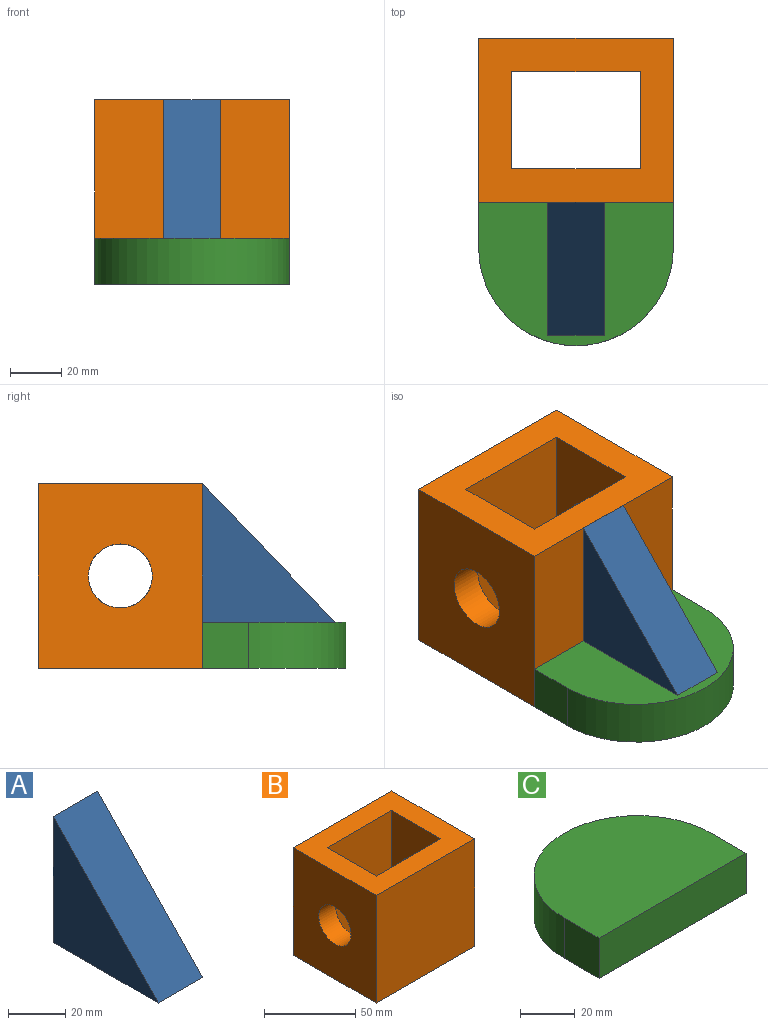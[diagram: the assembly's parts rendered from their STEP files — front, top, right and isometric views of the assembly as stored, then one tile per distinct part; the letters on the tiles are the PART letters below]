
ASSEMBLY  parts=3 mates=2
PART A: 5 faces, bbox 22x52x54 mm
  f0: plane 54x52mm, normal (0,-0.72,0.69), area 1649.3mm2, adj f1,f2,f3,f4
  f1: plane 52x22mm, normal (0,0,-1), area 1144mm2, adj f0,f2,f3,f4
  f2: plane 54x22mm, normal (0,1,0), area 1188mm2, adj f0,f1,f3,f4
  f3: plane 54x52mm, normal (1,0,0), area 1404mm2, adj f0,f1,f2
  f4: plane 54x52mm, normal (-1,0,0), area 1404mm2, adj f0,f1,f2
PART B: 12 faces, bbox 76x64x72 mm
  f0: plane 76x72mm, normal (0,-1,0), area 5472mm2, adj f1,f7,f8,f9
  f1: plane 72x64mm, normal (1,0,0), area 4117.1mm2, adj f0,f2,f8,f9,f11
  f2: plane 76x72mm, normal (0,1,0), area 5472mm2, adj f1,f7,f8,f9
  f3: plane 72x50mm, normal (0,-1,0), area 3600mm2, adj f4,f6,f8,f9
  f4: plane 72x38mm, normal (-1,0,0), area 2245.1mm2, adj f3,f5,f8,f9,f11
  f5: plane 72x50mm, normal (0,1,0), area 3600mm2, adj f4,f6,f8,f9
  f6: plane 72x38mm, normal (1,0,0), area 2245.1mm2, adj f3,f5,f8,f9,f10
  f7: plane 72x64mm, normal (-1,0,0), area 4117.1mm2, adj f0,f2,f8,f9,f10
  f8: plane 76x64mm, normal (0,0,1), area 2964mm2, adj f0,f1,f2,f3,f4,f5,f6,f7
  f9: plane 76x64mm, normal (0,0,-1), area 2964mm2, adj f0,f1,f2,f3,f4,f5,f6,f7
  f10: cylinder r=12.5mm len=25mm, axis (1,0,0), area 1021mm2, adj f6,f7
  f11: cylinder r=12.5mm len=25mm, axis (1,0,0), area 1021mm2, adj f1,f4
PART C: 6 faces, bbox 76x56x18 mm
  f0: cylinder r=38mm len=76mm, axis (0,0,-1), area 2148.8mm2, adj f1,f2,f3,f4
  f1: plane 76x56mm, normal (0,0,1), area 3636.2mm2, adj f0,f3,f4,f5
  f2: plane 76x56mm, normal (0,0,-1), area 3636.2mm2, adj f0,f3,f4,f5
  f3: plane 18x18mm, normal (1,0,0), area 324mm2, adj f0,f1,f2,f5
  f4: plane 18x18mm, normal (-1,0,0), area 324mm2, adj f0,f1,f2,f5
  f5: plane 76x18mm, normal (0,-1,0), area 1368mm2, adj f1,f2,f3,f4
PLACE A t=(6.63,-49.26,18.85)mm
PLACE B t=(-20.37,2.74,0.85)mm
PLACE C rot(axis=(0,0,1),180deg) t=(17.63,-15.26,0.85)mm
MATE planar C.f5 <-> B.f0  axis (0,1,0) through (17.63,2.74,0.85)mm
MATE planar A.f2 <-> B.f0  axis (0,1,0) through (17.63,2.74,72.85)mm
